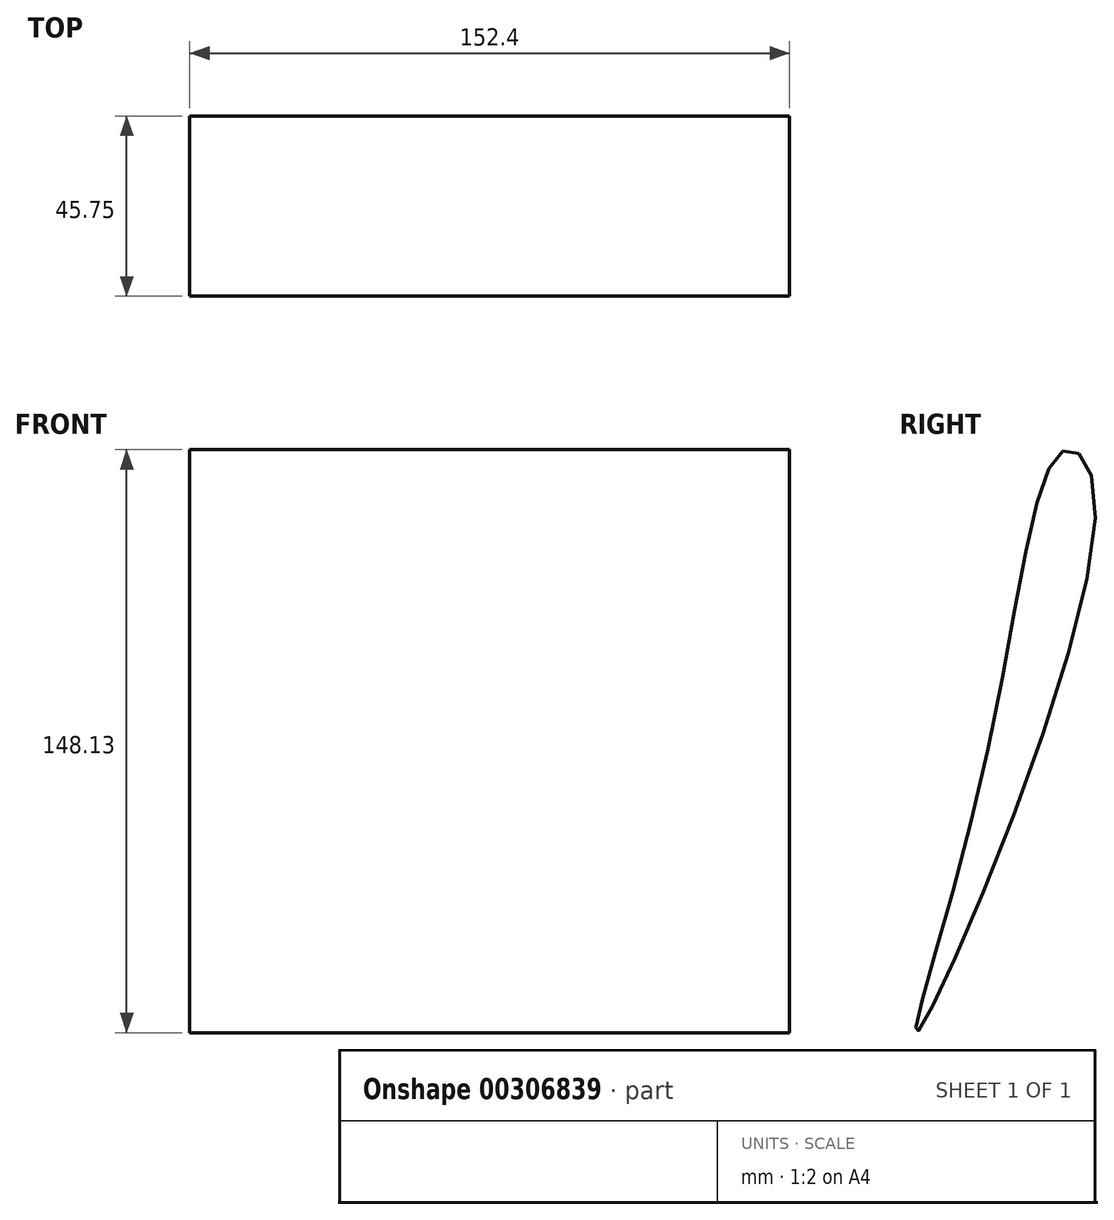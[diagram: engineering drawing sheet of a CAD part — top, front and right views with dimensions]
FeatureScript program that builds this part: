
annotation { "Feature Type Name" : "Feature", "Feature Type Description" : "" }
export const myFeature = defineFeature(function(context is Context, id is Id, definition is map)
    precondition{}
    {
        {
            var Q0;
            Q0=qCreatedBy(makeId("Right.planeOp"),FACE);
            var sketch = newSketch(context, id + "F0", { "sketchPlane" : qUnion([Q0])});
            skFitSpline(sketch, "E0", {"points": [v(34.7, 70.83) * mm, v(42.97, 55.32) * mm, v(-2.03, -76.46) * mm, v(14.34, -10.78) * mm, v(34.7, 70.83) * mm]});
            skSolve(sketch);
        }
        {
            var Q0;
            Q0=makeQuery(id+"F0.imprint","IMPRINT",FACE,{"disambiguationData":[TD([[makeQuery(id+"F0.imprint","IMPRINT",EDGE,{"derivedFrom":sQuery(id+"F0.wireOp",EDGE,"E0")}),-1.0]])]});
            extrude(context, id + "F1", {"entities" : qUnion([Q0]), "depth" : 76.2 * mm, "hasSecondDirection" : true, "secondDirectionOppositeDirection" : true, "secondDirectionDepth" : 76.2 * mm});
        }
    });
